# Revit family: ELVIRE RAIL SHOWER WITH OVERHEAD
name_source: partatom
category: Plumbing Fixtures
revit_build: Autodesk Revit 2016 (Build: 20161004_0715(x64)
units: mm (PartAtom-declared; Revit-internal decimal feet)

## family parameters
Cut with Voids When Loaded = No
Host = Face
OmniClass Number = 23.45.05.14.17
OmniClass Title = Showers
Part Type = Normal
Room Calculation Point = No
Round Connector Dimension = Use Diameter
Shared = No

## types (1)
- ELVIRE RAIL SHOWER WITH OVERHEAD 300MM - GUNMETAL
    Assembly Code = D2010710
    CW Connection = Yes
    Default Elevation = 0 mm  [stored 0 ft]
    Description = ELVIRE RAIL SHOWER WITH OVERHEAD 300MM - GUNMETAL
    HW Connection = Yes
    Manufacturer = GWA Bathrooms & Kitchens
    Material_Nozzles = GWA-Plastic-White
    Material_Rail = GWA-Metal-Gunmetal Grey
    Model = CAEL0042GM3A
    URL = https://www.caroma.com.au
    Vent Connection = No
    WELSRating_ANZRS = WELS 3 (Range D) Rated, 9L/min
    Waste Connection = No

note: [stored X ft] marks values corroborated as IEEE doubles in the binary element streams (Revit-internal decimal feet)

## geometry (parser evidence)
native form markers: Blend x4, Sweep x1
no freeform markers — native parametric forms only
